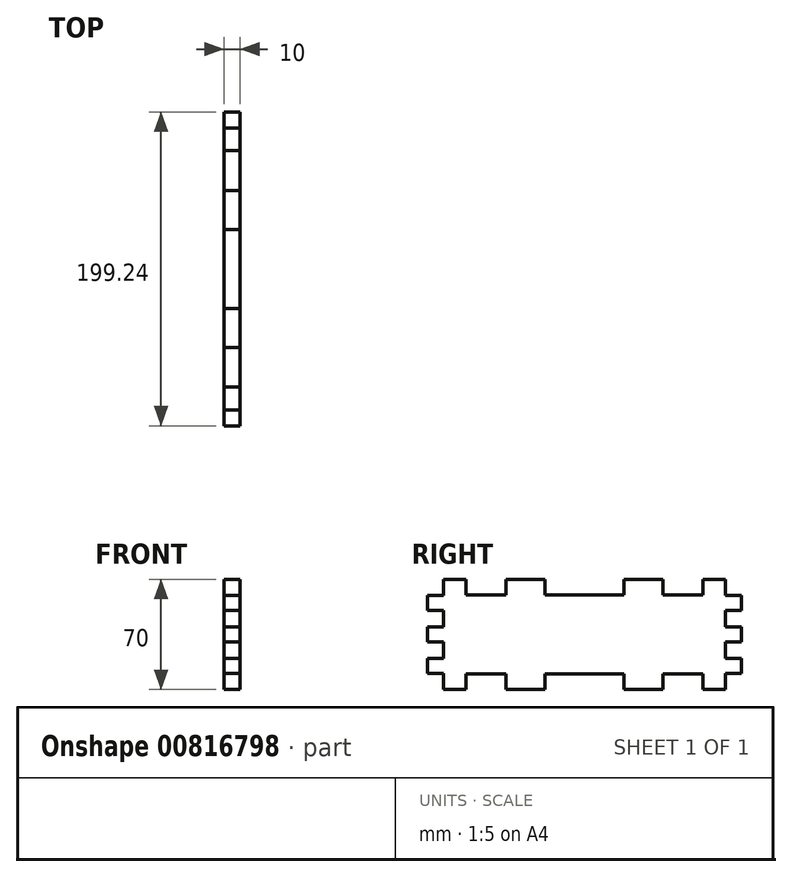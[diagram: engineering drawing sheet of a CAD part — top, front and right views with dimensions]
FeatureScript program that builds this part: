
annotation { "Feature Type Name" : "Feature", "Feature Type Description" : "" }
export const myFeature = defineFeature(function(context is Context, id is Id, definition is map)
    precondition{}
    {
        {
            var Q0;
            Q0=qCreatedBy(makeId("Right.planeOp"),FACE);
            var sketch = newSketch(context, id + "F0", { "sketchPlane" : qUnion([Q0])});
            skPoint(sketch, "E0.middle", {"position": v(0, 0) * mm});
            skLineSegment(sketch, "E1", {"start": v(-89.63, -24.87) * mm, "end": v(-89.62, -35) * mm});
            skLineSegment(sketch, "E2", {"start": v(-89.62, -24.87) * mm, "end": v(-99.63, -24.87) * mm});
            skLineSegment(sketch, "E3", {"start": v(-99.63, -24.87) * mm, "end": v(-99.63, -15.12) * mm});
            skLineSegment(sketch, "E4", {"start": v(-99.63, -15.12) * mm, "end": v(-89.63, -15.12) * mm});
            skLineSegment(sketch, "E5", {"start": v(-89.63, -15.13) * mm, "end": v(-89.63, -4.87) * mm});
            skLineSegment(sketch, "E6", {"start": v(-89.63, -4.87) * mm, "end": v(-99.63, -4.87) * mm});
            skLineSegment(sketch, "E7", {"start": v(-99.63, -4.87) * mm, "end": v(-99.63, 0) * mm});
            skLineSegment(sketch, "E8.MirrorCS", {"start": v(-99.63, 4.87) * mm, "end": v(-99.63, 0) * mm});
            skLineSegment(sketch, "E9.MirrorCS", {"start": v(-89.63, 4.87) * mm, "end": v(-99.63, 4.87) * mm});
            skLineSegment(sketch, "E10.MirrorCS", {"start": v(-89.63, 15.12) * mm, "end": v(-89.63, 4.87) * mm});
            skLineSegment(sketch, "E11.MirrorCS", {"start": v(-99.63, 15.13) * mm, "end": v(-89.63, 15.13) * mm});
            skLineSegment(sketch, "E12.MirrorCS", {"start": v(-99.63, 24.87) * mm, "end": v(-99.63, 15.12) * mm});
            skLineSegment(sketch, "E13.MirrorCS", {"start": v(-89.62, 24.87) * mm, "end": v(-99.63, 24.87) * mm});
            skLineSegment(sketch, "E14.MirrorCS", {"start": v(-89.63, 24.87) * mm, "end": v(-89.62, 35) * mm});
            skLineSegment(sketch, "E15.MirrorCS", {"start": v(99.63, 4.87) * mm, "end": v(99.63, 0) * mm});
            skLineSegment(sketch, "E16.MirrorCS", {"start": v(99.63, -4.87) * mm, "end": v(99.63, 0) * mm});
            skLineSegment(sketch, "E17.MirrorCS", {"start": v(89.62, 24.87) * mm, "end": v(99.63, 24.87) * mm});
            skLineSegment(sketch, "E18.MirrorCS", {"start": v(89.62, -24.88) * mm, "end": v(99.63, -24.88) * mm});
            skLineSegment(sketch, "E19.MirrorCS", {"start": v(89.63, -24.87) * mm, "end": v(89.62, -35) * mm});
            skLineSegment(sketch, "E20.MirrorCS", {"start": v(99.63, -24.87) * mm, "end": v(99.63, -15.12) * mm});
            skLineSegment(sketch, "E21.MirrorCS", {"start": v(99.63, 24.87) * mm, "end": v(99.63, 15.12) * mm});
            skLineSegment(sketch, "E22.MirrorCS", {"start": v(89.63, 15.12) * mm, "end": v(89.63, 4.87) * mm});
            skLineSegment(sketch, "E23.MirrorCS", {"start": v(99.63, 15.13) * mm, "end": v(89.63, 15.13) * mm});
            skLineSegment(sketch, "E24.MirrorCS", {"start": v(89.63, 4.88) * mm, "end": v(99.63, 4.88) * mm});
            skLineSegment(sketch, "E25.MirrorCS", {"start": v(99.63, -15.13) * mm, "end": v(89.63, -15.13) * mm});
            skLineSegment(sketch, "E26.MirrorCS", {"start": v(89.63, -4.88) * mm, "end": v(99.63, -4.88) * mm});
            skLineSegment(sketch, "E27.MirrorCS", {"start": v(89.63, 24.87) * mm, "end": v(89.62, 35) * mm});
            skLineSegment(sketch, "E28.MirrorCS", {"start": v(89.63, -15.12) * mm, "end": v(89.63, -4.87) * mm});
            skLineSegment(sketch, "E29", {"start": v(-89.62, -35) * mm, "end": v(-75.13, -35) * mm});
            skLineSegment(sketch, "E30", {"start": v(-75.13, -35) * mm, "end": v(-75.13, -25) * mm});
            skLineSegment(sketch, "E31", {"start": v(-75.13, -25) * mm, "end": v(-49.87, -25) * mm});
            skLineSegment(sketch, "E32", {"start": v(-49.87, -25) * mm, "end": v(-49.87, -35) * mm});
            skLineSegment(sketch, "E33", {"start": v(-49.87, -35) * mm, "end": v(-25.12, -35) * mm});
            skLineSegment(sketch, "E34", {"start": v(-25.12, -35) * mm, "end": v(-25.12, -25) * mm});
            skLineSegment(sketch, "E35", {"start": v(-25.12, -25) * mm, "end": v(0, -25) * mm});
            skLineSegment(sketch, "E36.MirrorCS", {"start": v(89.62, -35) * mm, "end": v(75.13, -35) * mm});
            skLineSegment(sketch, "E37.MirrorCS", {"start": v(75.13, -35) * mm, "end": v(75.13, -25) * mm});
            skLineSegment(sketch, "E38.MirrorCS", {"start": v(75.13, -25) * mm, "end": v(49.87, -25) * mm});
            skLineSegment(sketch, "E39.MirrorCS", {"start": v(49.87, -25) * mm, "end": v(49.87, -35) * mm});
            skLineSegment(sketch, "E40.MirrorCS", {"start": v(49.87, -35) * mm, "end": v(25.12, -35) * mm});
            skLineSegment(sketch, "E41.MirrorCS", {"start": v(25.12, -35) * mm, "end": v(25.12, -25) * mm});
            skLineSegment(sketch, "E42.MirrorCS", {"start": v(25.12, -25) * mm, "end": v(0, -25) * mm});
            skLineSegment(sketch, "E43.MirrorCS", {"start": v(-89.62, 35) * mm, "end": v(-75.13, 35) * mm});
            skLineSegment(sketch, "E44.MirrorCS", {"start": v(-75.13, 35) * mm, "end": v(-75.13, 25) * mm});
            skLineSegment(sketch, "E45.MirrorCS", {"start": v(-75.13, 25) * mm, "end": v(-49.87, 25) * mm});
            skLineSegment(sketch, "E46.MirrorCS", {"start": v(-49.87, 25) * mm, "end": v(-49.87, 35) * mm});
            skLineSegment(sketch, "E47.MirrorCS", {"start": v(-49.87, 35) * mm, "end": v(-25.12, 35) * mm});
            skLineSegment(sketch, "E48.MirrorCS", {"start": v(-25.12, 35) * mm, "end": v(-25.12, 25) * mm});
            skLineSegment(sketch, "E49.MirrorCS", {"start": v(-25.12, 25) * mm, "end": v(0, 25) * mm});
            skLineSegment(sketch, "E50.MirrorCS", {"start": v(25.12, 25) * mm, "end": v(0, 25) * mm});
            skLineSegment(sketch, "E51.MirrorCS", {"start": v(25.12, 35) * mm, "end": v(25.12, 25) * mm});
            skLineSegment(sketch, "E52.MirrorCS", {"start": v(49.87, 35) * mm, "end": v(25.12, 35) * mm});
            skLineSegment(sketch, "E53.MirrorCS", {"start": v(49.87, 25) * mm, "end": v(49.87, 35) * mm});
            skLineSegment(sketch, "E54.MirrorCS", {"start": v(75.13, 25) * mm, "end": v(49.87, 25) * mm});
            skLineSegment(sketch, "E55.MirrorCS", {"start": v(75.13, 35) * mm, "end": v(75.13, 25) * mm});
            skLineSegment(sketch, "E56.MirrorCS", {"start": v(89.62, 35) * mm, "end": v(75.13, 35) * mm});
            skSolve(sketch);
        }
        {
            var Q0;
            Q0=makeQuery(id+"F0.imprint","IMPRINT",FACE,{"disambiguationData":[TD([[makeQuery(id+"F0.imprint","IMPRINT",EDGE,{"derivedFrom":sQuery(id+"F0.wireOp",EDGE,"E1")}),1.0]])]});
            extrude(context, id + "F1", {"entities" : qUnion([Q0]), "depth" : 10 * mm, "offsetDistance" : 25 * mm});
        }
    });
